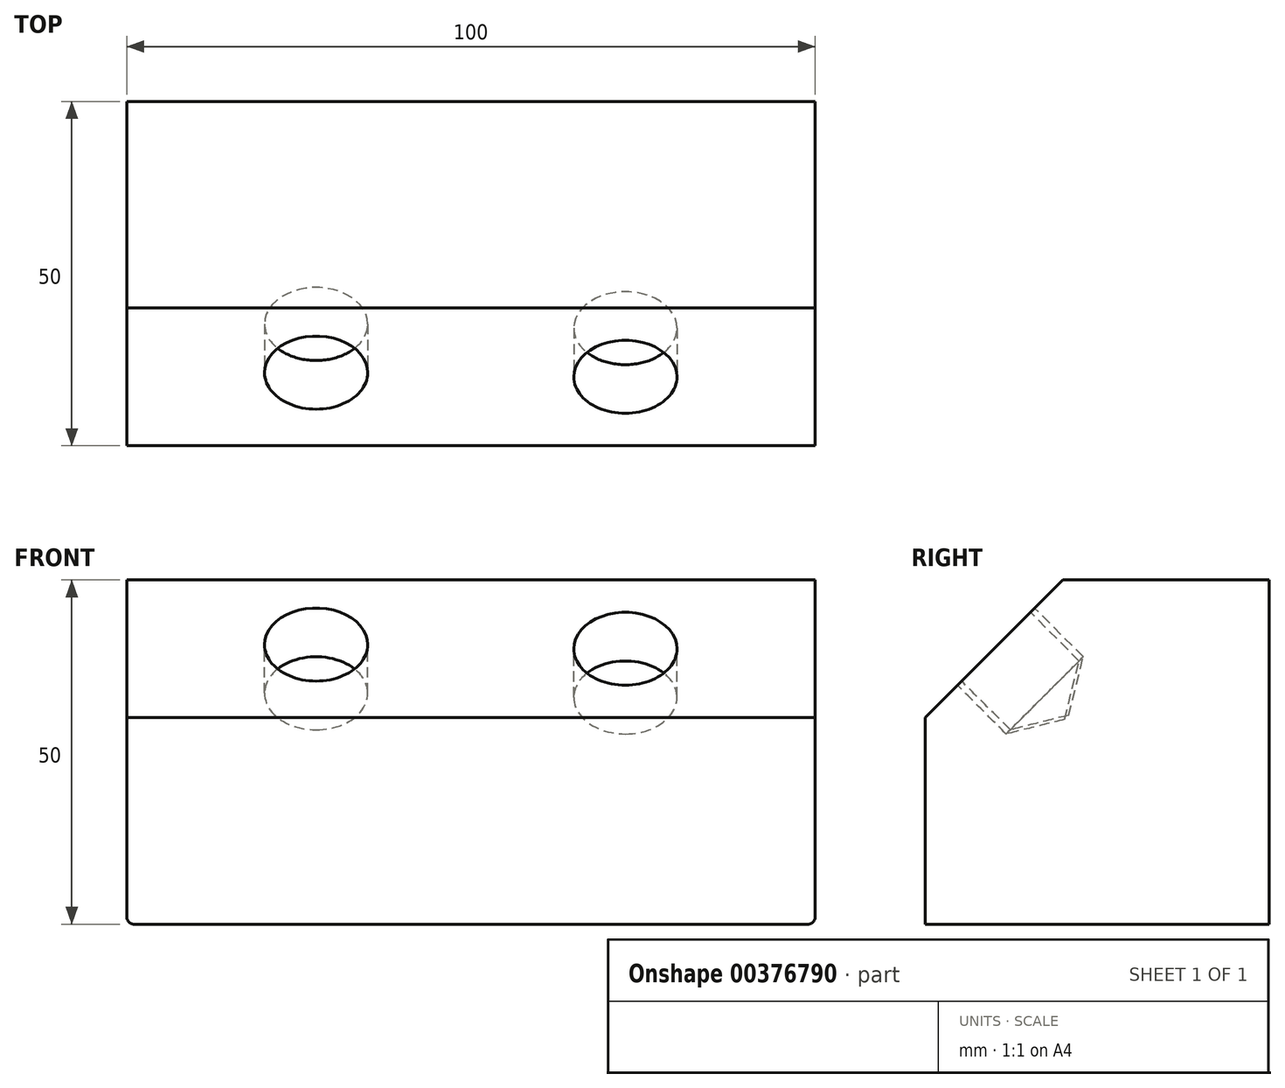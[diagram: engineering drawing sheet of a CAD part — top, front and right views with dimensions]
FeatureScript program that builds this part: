
annotation { "Feature Type Name" : "Feature", "Feature Type Description" : "" }
export const myFeature = defineFeature(function(context is Context, id is Id, definition is map)
    precondition{}
    {
        {
            var Q0;
            Q0=qCreatedBy(makeId("Top.planeOp"),FACE);
            var sketch = newSketch(context, id + "F0", { "sketchPlane" : qUnion([Q0])});
            skLineSegment(sketch, "E0.bottom", {"start": v(0, 0) * mm, "end": v(-100, 0) * mm});
            skLineSegment(sketch, "E0.top", {"start": v(0, -50) * mm, "end": v(-100, -50) * mm});
            skLineSegment(sketch, "E0.left", {"start": v(0, 0) * mm, "end": v(0, -50) * mm});
            skLineSegment(sketch, "E0.right", {"start": v(-100, 0) * mm, "end": v(-100, -50) * mm});
            skSolve(sketch);
        }
        {
            var Q0;
            Q0 = qSketchRegion(id + "F0", true);
            extrude(context, id + "F1", {"entities" : qUnion([Q0]), "depth" : 50 * mm});
        }
        {
            var Q0;
            Q0=makeQuery(id+"F1.opExtrude","CAP_EDGE",EDGE,{"disambiguationData":[OSD([sQuery(id+"F0.wireOp",EDGE,"E0.top")])],"isStart":false});
            chamfer(context, id + "F2", {"entities" : qUnion([Q0]), "width" : 20 * mm, "tangentPropagation" : true});
        }
        {
            var Q0;
            Q0=makeQuery(id+"F2.opChamfer","BLEND_FACE",FACE,{"disambiguationData":[OSD([sQuery(id+"F0.wireOp",EDGE,"E0.top")])]});
            var sketch = newSketch(context, id + "F3", { "sketchPlane" : qUnion([Q0])});
            skCircle(sketch, "E1", {"center": v(-27.5, 0.86) * mm, "radius": 7.5 * mm});
            skCircle(sketch, "E2", {"center": v(-72.5, 0.86) * mm, "radius": 7.5 * mm});
            skSolve(sketch);
        }
        {
            var Q0;
            Q0=makeQuery(id+"F3.imprint","IMPRINT",FACE,{"disambiguationData":[TD([[makeQuery(id+"F3.imprint","IMPRINT",EDGE,{"derivedFrom":sQuery(id+"F3.wireOp",EDGE,"E1")}),-1.0]])]});
            var sketch = newSketch(context, id + "F4", { "sketchPlane" : qUnion([Q0])});
            skPoint(sketch, "E3", {"position": v(-27.56, 0) * mm});
            skPoint(sketch, "E4", {"position": v(-73.02, 0) * mm});
            skSolve(sketch);
        }
        {
            var Q0;
            Q0=sQuery(id+"F4.wireOp",VERTEX,"E3");
            var Q1;
            Q1=makeQuery(id+"F1.opExtrude","SWEPT_BODY",BODY,{"disambiguationData":[OSD([sQuery(id+"F0.wireOp",EDGE,"E0.bottom"),sQuery(id+"F0.wireOp",EDGE,"E0.top"),sQuery(id+"F0.wireOp",EDGE,"E0.left"),sQuery(id+"F0.wireOp",EDGE,"E0.right")])]});
            hole(context, id + "F5", {"style" : HoleStyle.SIMPLE, "endStyle" : HoleEndStyle.BLIND, "holeDiameter" : 15 * mm, "holeDepth" : 10 * mm, "isTappedThrough" : true, "tappedDepth" : 12 * mm, "tapClearance" : 3, "locations" : qUnion([Q0]), "scope" : qUnion([Q1])});
        }
        {
            var Q0;
            Q0=sQuery(id+"F3.wireOp",VERTEX,"E2.center");
            var Q1;
            Q1=makeQuery(id+"F1.opExtrude","SWEPT_BODY",BODY,{"disambiguationData":[OSD([sQuery(id+"F0.wireOp",EDGE,"E0.bottom"),sQuery(id+"F0.wireOp",EDGE,"E0.top"),sQuery(id+"F0.wireOp",EDGE,"E0.left"),sQuery(id+"F0.wireOp",EDGE,"E0.right")])]});
            hole(context, id + "F6", {"style" : HoleStyle.SIMPLE, "endStyle" : HoleEndStyle.BLIND, "holeDiameter" : 15 * mm, "holeDepth" : 10 * mm, "isTappedThrough" : true, "tappedDepth" : 12 * mm, "tapClearance" : 3, "locations" : qUnion([Q0]), "scope" : qUnion([Q1])});
        }
        {
            var Q0;
            Q0=makeQuery(id+"F1.opExtrude","CAP_EDGE",EDGE,{"disambiguationData":[OSD([sQuery(id+"F0.wireOp",EDGE,"E0.left")])],"isStart":true});
            var Q1;
            Q1=makeQuery(id+"F1.opExtrude","CAP_EDGE",EDGE,{"disambiguationData":[OSD([sQuery(id+"F0.wireOp",EDGE,"E0.right")])],"isStart":true});
            fillet(context, id + "F7", {"entities" : qUnion([Q0, Q1]), "radius" : 1 * mm, "tangentPropagation" : true, "allowEdgeOverflow" : false});
        }
    });
